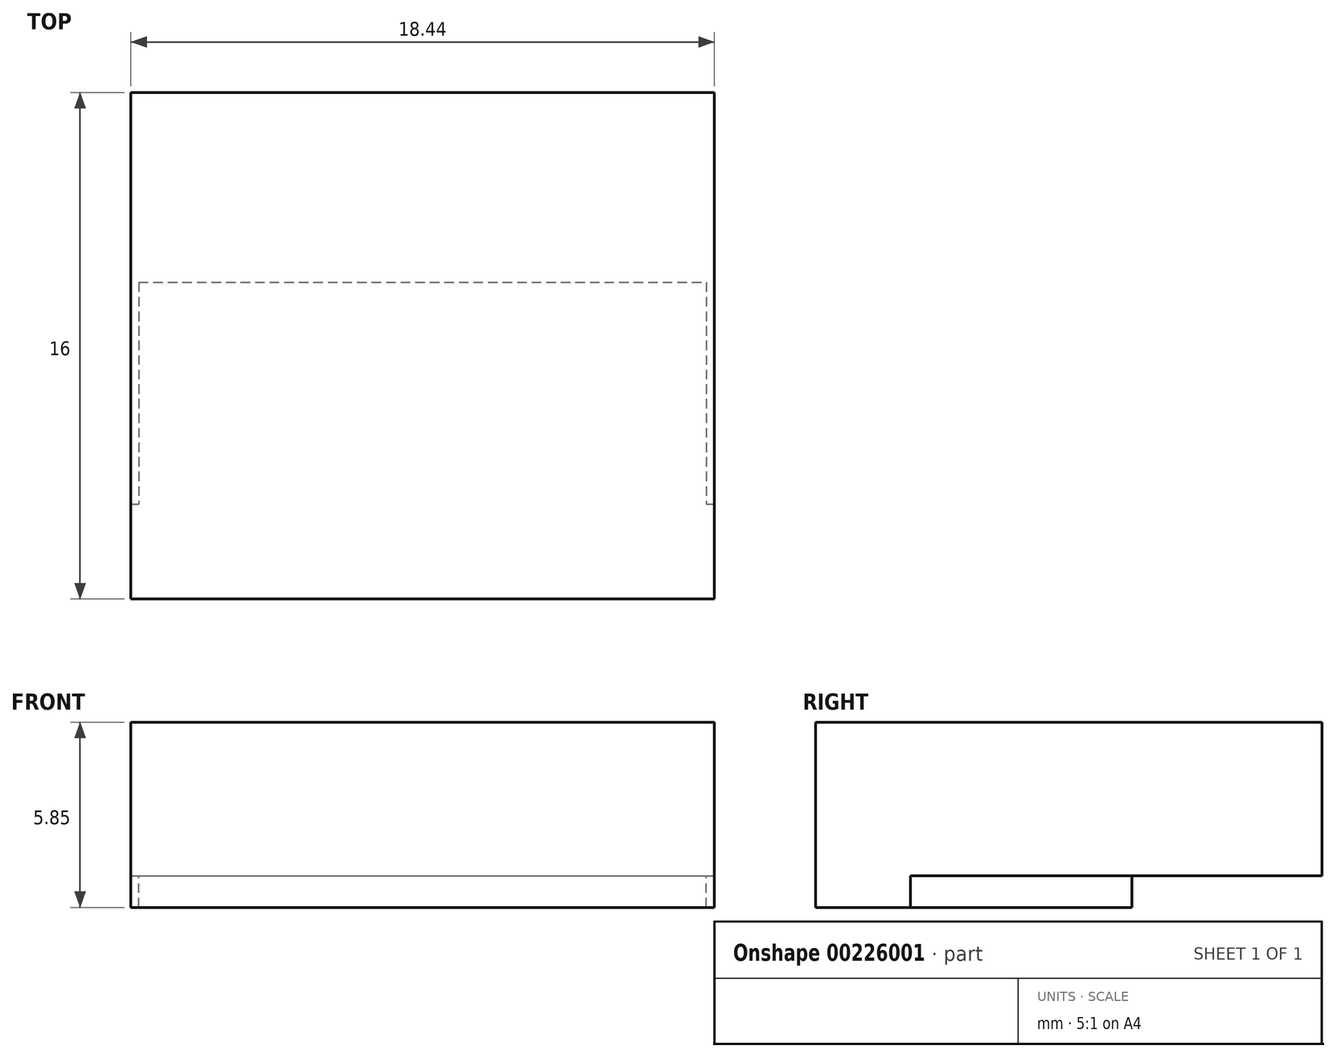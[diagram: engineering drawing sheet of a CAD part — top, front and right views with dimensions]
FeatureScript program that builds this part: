
annotation { "Feature Type Name" : "Feature", "Feature Type Description" : "" }
export const myFeature = defineFeature(function(context is Context, id is Id, definition is map)
    precondition{}
    {
        {
            var Q0;
            Q0=qCreatedBy(makeId("Top.planeOp"),FACE);
            var sketch = newSketch(context, id + "F0", { "sketchPlane" : qUnion([Q0])});
            skLineSegment(sketch, "E0.bottom", {"start": v(0, 0) * mm, "end": v(18.44, 0) * mm});
            skLineSegment(sketch, "E0.top", {"start": v(0, 13) * mm, "end": v(18.44, 13) * mm});
            skLineSegment(sketch, "E0.left", {"start": v(0, 0) * mm, "end": v(0, 13) * mm});
            skLineSegment(sketch, "E0.right", {"start": v(18.44, 0) * mm, "end": v(18.44, 13) * mm});
            skSolve(sketch);
        }
        {
            var Q0;
            Q0 = qSketchRegion(id + "F0", true);
            extrude(context, id + "F1", {"entities" : qUnion([Q0]), "depth" : 4.85 * mm});
        }
        {
            var Q0;
            Q0=makeQuery(id+"F1.opExtrude","CAP_FACE",FACE,{"disambiguationData":[OSD([sQuery(id+"F0.wireOp",EDGE,"E0.bottom"),sQuery(id+"F0.wireOp",EDGE,"E0.top"),sQuery(id+"F0.wireOp",EDGE,"E0.left"),sQuery(id+"F0.wireOp",EDGE,"E0.right")])],"isStart":true});
            var sketch = newSketch(context, id + "F2", { "sketchPlane" : qUnion([Q0])});
            skLineSegment(sketch, "E1.bottom", {"start": v(0.25, -7) * mm, "end": v(1.25, -7) * mm});
            skLineSegment(sketch, "E1.top", {"start": v(0.25, 0) * mm, "end": v(1.25, 0) * mm});
            skLineSegment(sketch, "E1.left", {"start": v(0.25, -7) * mm, "end": v(0.25, 0) * mm});
            skLineSegment(sketch, "E1.right", {"start": v(1.25, -7) * mm, "end": v(1.25, 0) * mm});
            skLineSegment(sketch, "E2", {"start": v(9.22, 0) * mm, "end": v(9.22, -13) * mm, "construction": true});
            skLineSegment(sketch, "E3.MirrorCS", {"start": v(17.19, -7) * mm, "end": v(17.19, 0) * mm});
            skLineSegment(sketch, "E4.MirrorCS", {"start": v(18.19, -7) * mm, "end": v(18.19, 0) * mm});
            skLineSegment(sketch, "E5.MirrorCS", {"start": v(18.2, 0) * mm, "end": v(17.19, 0) * mm});
            skLineSegment(sketch, "E6.MirrorCS", {"start": v(18.2, -7) * mm, "end": v(17.2, -7) * mm});
            skSolve(sketch);
        }
        {
            var Q0;
            Q0 = qSketchRegion(id + "F2", true);
            extrude(context, id + "F3", {"entities" : qUnion([Q0]), "operationType" : NewBodyOperationType.ADD, "depth" : 1 * mm});
        }
        {
            var Q0;
            Q0=makeQuery(id+"F1.opExtrude","SWEPT_FACE",FACE,{"disambiguationData":[OSD([sQuery(id+"F0.wireOp",EDGE,"E0.bottom")])]});
            var sketch = newSketch(context, id + "F4", { "sketchPlane" : qUnion([Q0])});
            skLineSegment(sketch, "E7.0", {"start": v(0, 4.85) * mm, "end": v(18.44, 4.85) * mm});
            skLineSegment(sketch, "E8", {"start": v(0, 4.85) * mm, "end": v(0, -1) * mm});
            skLineSegment(sketch, "E9", {"start": v(18.44, -1) * mm, "end": v(0, -1) * mm});
            skLineSegment(sketch, "E10", {"start": v(18.44, -1) * mm, "end": v(18.44, 4.85) * mm});
            skSolve(sketch);
        }
        {
            var Q0;
            Q0 = qSketchRegion(id + "F4", true);
            extrude(context, id + "F5", {"entities" : qUnion([Q0]), "depth" : 3 * mm});
        }
        {
            var Q0;
            Q0=makeQuery(id+"F5.opExtrude","CAP_FACE",FACE,{"disambiguationData":[OSD([sQuery(id+"F4.wireOp",EDGE,"E7.0"),sQuery(id+"F4.wireOp",EDGE,"E8"),sQuery(id+"F4.wireOp",EDGE,"E9"),sQuery(id+"F4.wireOp",EDGE,"E10")])],"isStart":true});
            var sketch = newSketch(context, id + "F6", { "sketchPlane" : qUnion([Q0])});
            skLineSegment(sketch, "E11.0", {"start": v(-17.19, -1) * mm, "end": v(-1.25, -1) * mm});
            skLineSegment(sketch, "E12.0", {"start": v(-1.25, 0) * mm, "end": v(-17.19, 0) * mm});
            skLineSegment(sketch, "E13.0", {"start": v(-17.19, -1) * mm, "end": v(-17.19, 0) * mm});
            skLineSegment(sketch, "E14.0", {"start": v(-1.25, -1) * mm, "end": v(-1.25, 0) * mm});
            skSolve(sketch);
        }
        {
            var Q0;
            Q0 = qSketchRegion(id + "F6", true);
            var Q1;
            Q1=makeQuery(id+"F3.opExtrude","SWEPT_FACE",FACE,{"disambiguationData":[OSD([sQuery(id+"F2.wireOp",EDGE,"E1.bottom")])]});
            extrude(context, id + "F7", {"entities" : qUnion([Q0]), "operationType" : NewBodyOperationType.ADD, "endBound" : BoundingType.UP_TO_SURFACE, "endBoundEntityFace" : qUnion([Q1]), "depth" : 11 * mm, "offsetDistance" : 25 * mm});
        }
    });
